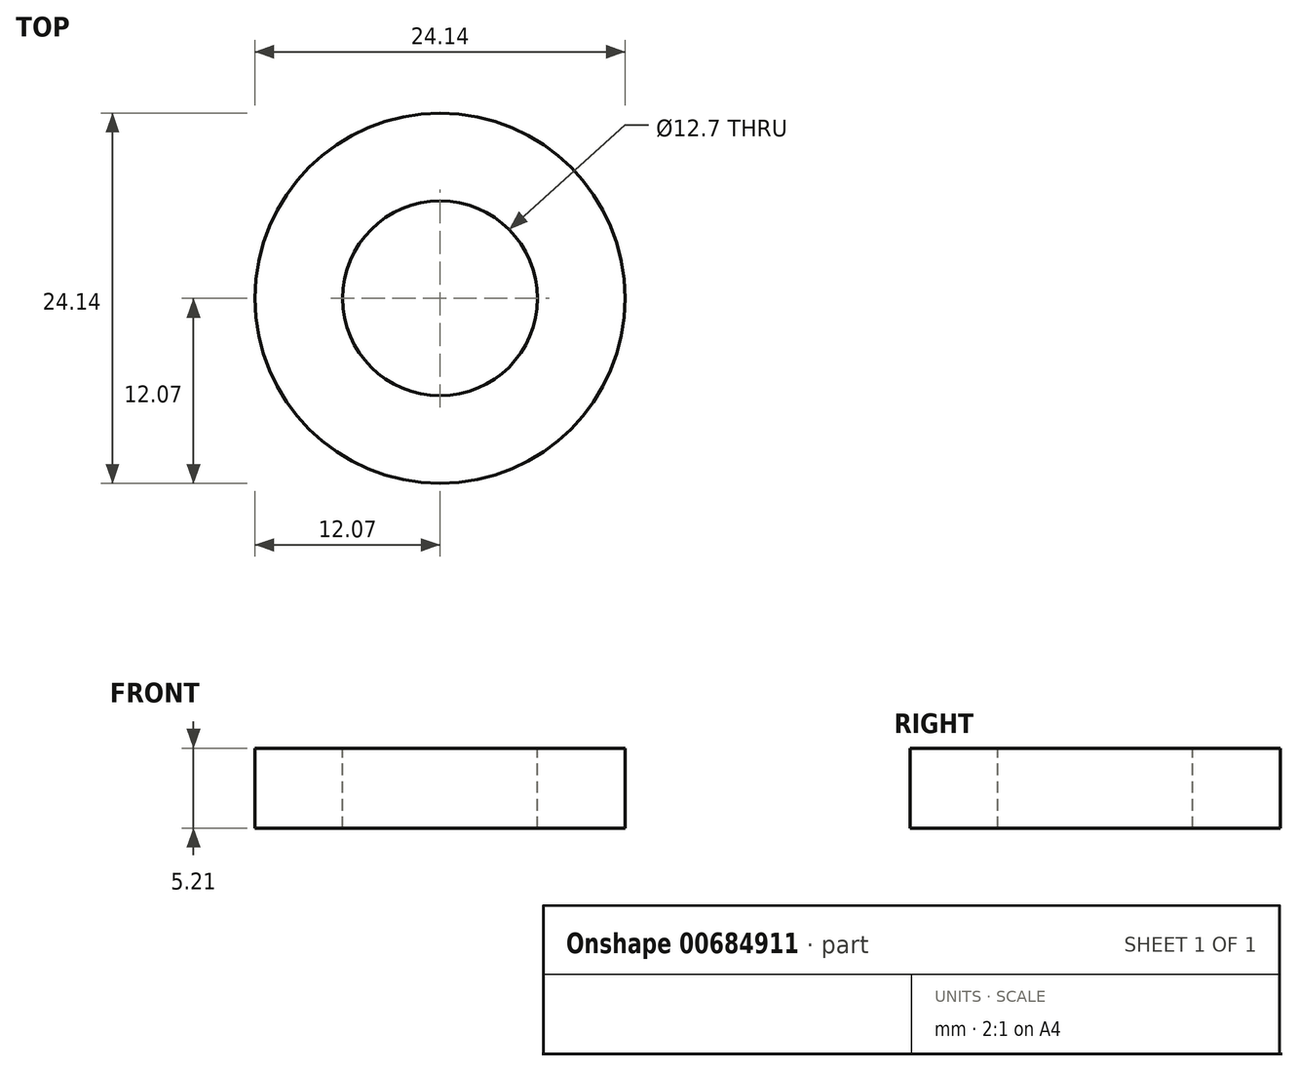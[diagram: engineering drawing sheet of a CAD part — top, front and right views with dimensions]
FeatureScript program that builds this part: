
annotation { "Feature Type Name" : "Feature", "Feature Type Description" : "" }
export const myFeature = defineFeature(function(context is Context, id is Id, definition is map)
    precondition{}
    {
        {
            var Q0;
            Q0=qCreatedBy(makeId("Front.planeOp"),FACE);
            var sketch = newSketch(context, id + "F0", { "sketchPlane" : qUnion([Q0])});
            skLineSegment(sketch, "E0", {"start": v(0, 17.53) * mm, "end": v(0, -18.25) * mm, "construction": true});
            skLineSegment(sketch, "E1", {"start": v(6.35, 5.2) * mm, "end": v(6.35, 0) * mm});
            skLineSegment(sketch, "E2", {"start": v(6.35, 0) * mm, "end": v(12.06, 0) * mm});
            skLineSegment(sketch, "E3", {"start": v(12.07, 0) * mm, "end": v(12.07, 5.2) * mm});
            skLineSegment(sketch, "E4", {"start": v(12.06, 5.2) * mm, "end": v(6.35, 5.2) * mm});
            skSolve(sketch);
        }
        {
            var Q0;
            Q0 = qSketchRegion(id + "F0", true);
            var Q1;
            Q1=sQuery(id+"F0.wireOp",EDGE,"E0");
            revolve(context, id + "F1", {"surfaceOperationType" : NewSurfaceOperationType.NEW, "entities" : qUnion([Q0]), "axis" : qUnion([Q1]), "revolveType" : RevolveType.FULL});
        }
    });
